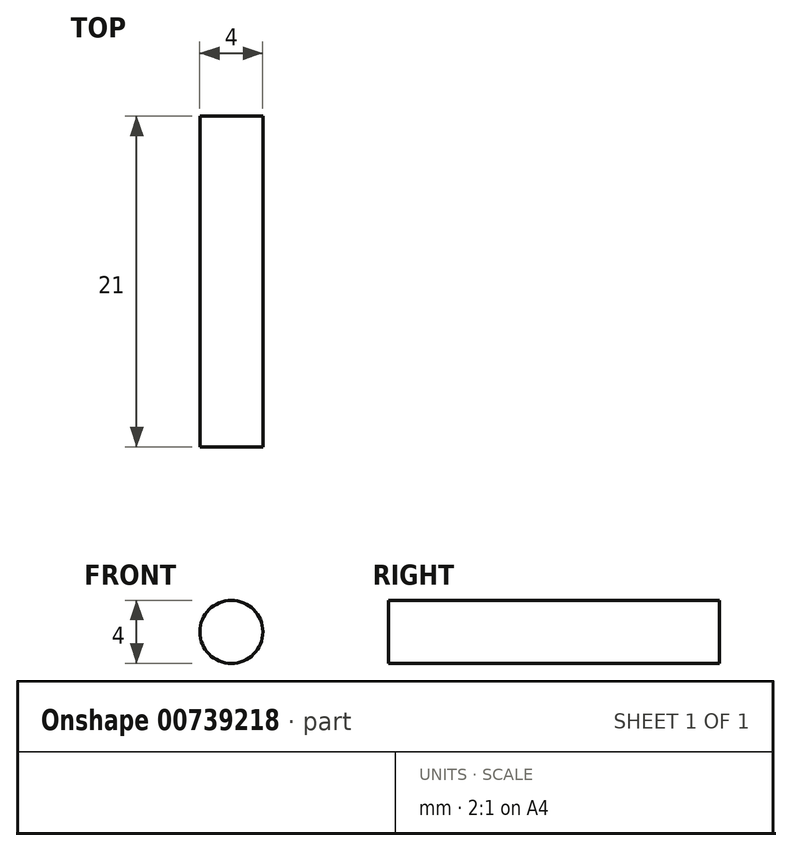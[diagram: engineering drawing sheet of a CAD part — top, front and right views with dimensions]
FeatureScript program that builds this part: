
annotation { "Feature Type Name" : "Feature", "Feature Type Description" : "" }
export const myFeature = defineFeature(function(context is Context, id is Id, definition is map)
    precondition{}
    {
        {
            var Q0;
            Q0=qCreatedBy(makeId("Front.planeOp"),FACE);
            var sketch = newSketch(context, id + "F0", { "sketchPlane" : qUnion([Q0])});
            skCircle(sketch, "E0", {"center": v(4.66, 13.39) * mm, "radius": 2 * mm});
            skSolve(sketch);
        }
        {
            var Q0;
            Q0 = qSketchRegion(id + "F0", true);
            extrude(context, id + "F1", {"entities" : qUnion([Q0]), "depth" : 21 * mm, "offsetDistance" : 25.4 * mm});
        }
    });
